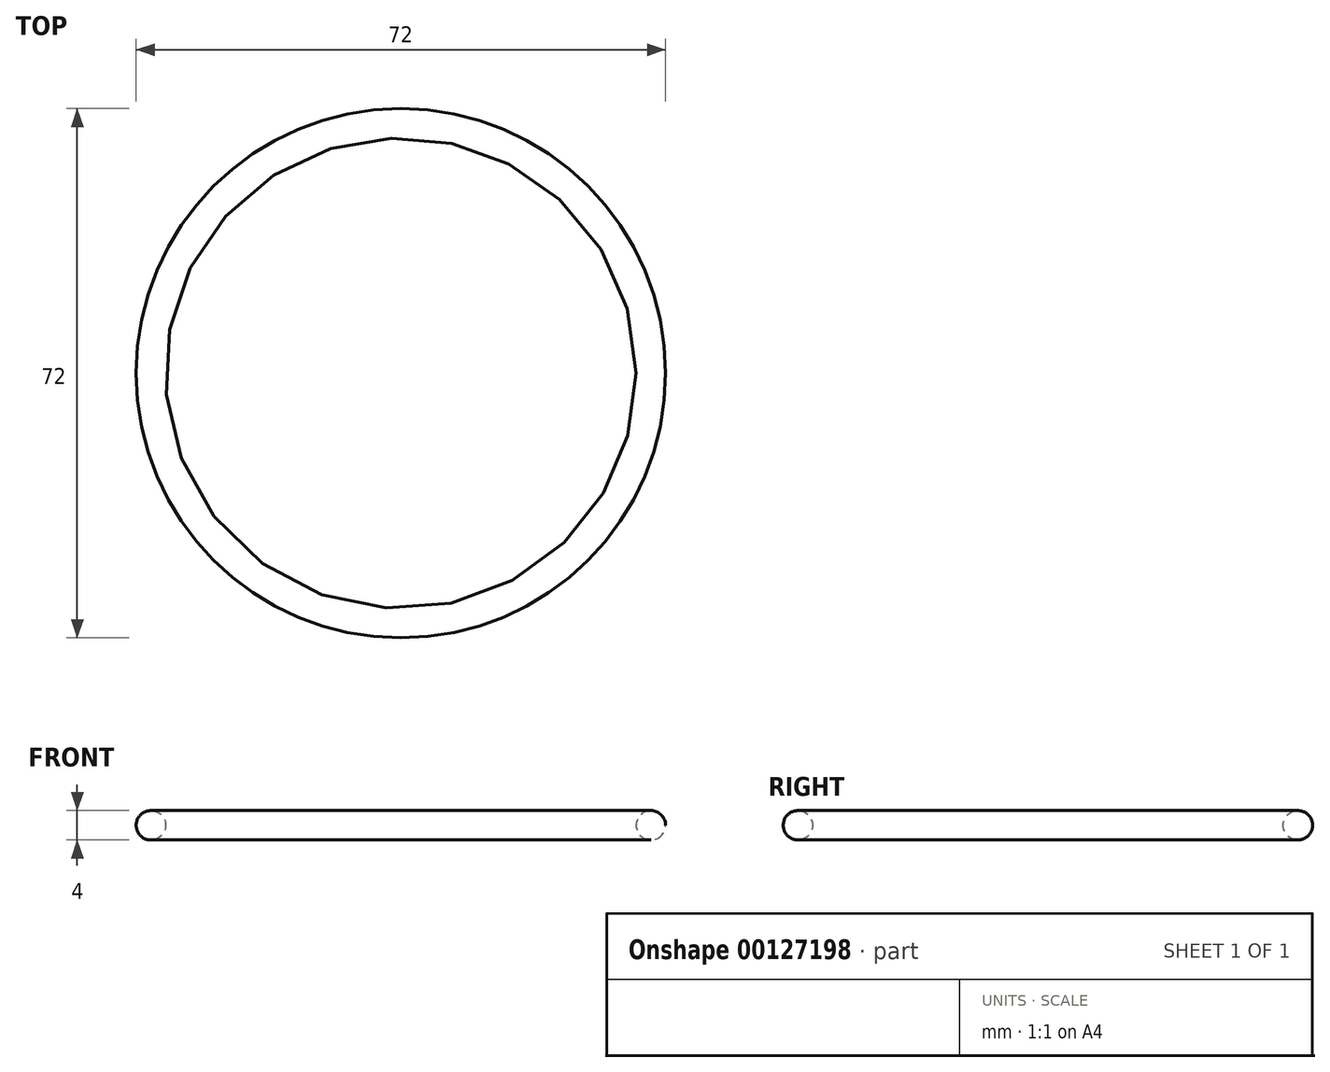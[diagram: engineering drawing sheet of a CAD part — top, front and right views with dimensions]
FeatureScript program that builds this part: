
annotation { "Feature Type Name" : "Feature", "Feature Type Description" : "" }
export const myFeature = defineFeature(function(context is Context, id is Id, definition is map)
    precondition{}
    {
        {
            var Q0;
            Q0=qCreatedBy(makeId("Top.planeOp"),FACE);
            var sketch = newSketch(context, id + "F0", { "sketchPlane" : qUnion([Q0])});
            skCircle(sketch, "E0", {"center": v(0, 0) * mm, "radius": 34 * mm});
            skPoint(sketch, "E1", {"position": v(-34, 0) * mm});
            skSolve(sketch);
        }
        {
            var Q0;
            Q0=qCreatedBy(makeId("Front.planeOp"),FACE);
            var sketch = newSketch(context, id + "F1", { "sketchPlane" : qUnion([Q0])});
            skCircle(sketch, "E2", {"center": v(-34, 0) * mm, "radius": 2 * mm});
            skSolve(sketch);
        }
        {
            var Q0;
            Q0=makeQuery(id+"F1.imprint","IMPRINT",FACE,{"disambiguationData":[TD([[makeQuery(id+"F1.imprint","IMPRINT",EDGE,{"derivedFrom":sQuery(id+"F1.wireOp",EDGE,"E2")}),1.0]])]});
            var Q1;
            Q1=sQuery(id+"F0.wireOp",EDGE,"E0");
            sweep(context, id + "F2", {"profiles" : qUnion([Q0]), "path" : qUnion([Q1])});
        }
    });
